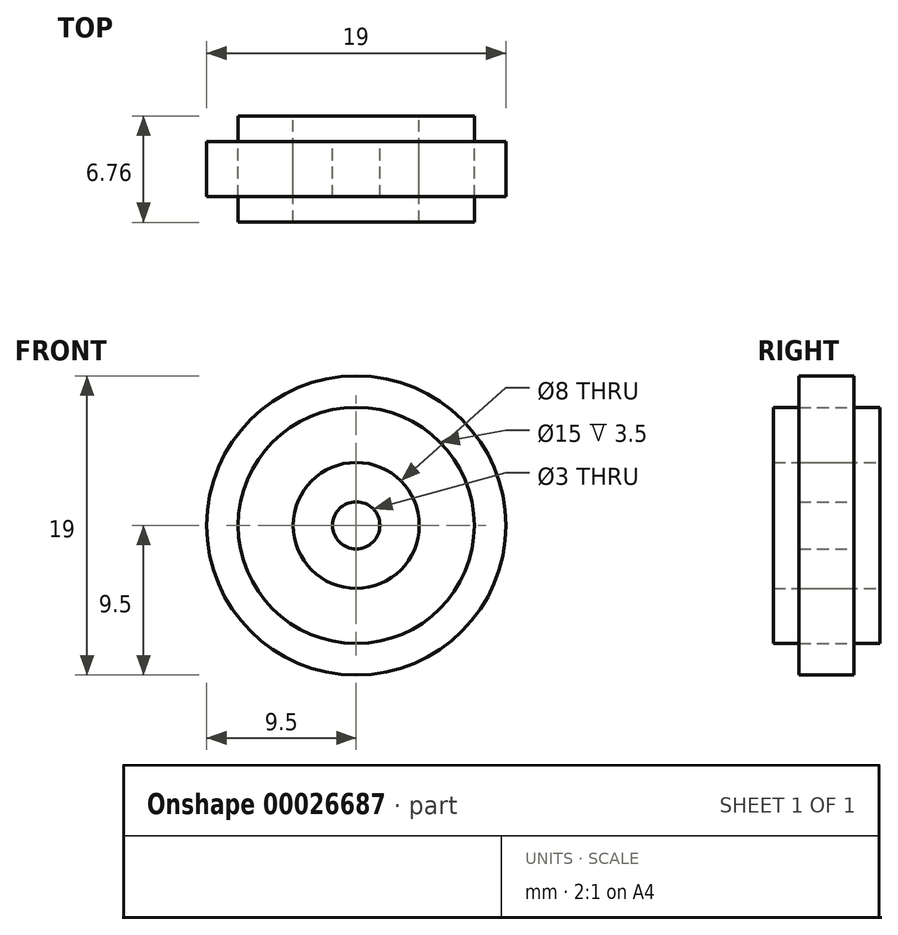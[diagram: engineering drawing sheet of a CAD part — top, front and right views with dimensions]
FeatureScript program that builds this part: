
annotation { "Feature Type Name" : "Feature", "Feature Type Description" : "" }
export const myFeature = defineFeature(function(context is Context, id is Id, definition is map)
    precondition{}
    {
        {
            var Q0;
            Q0=qCreatedBy(makeId("Front.planeOp"),FACE);
            var sketch = newSketch(context, id + "F0", { "sketchPlane" : qUnion([Q0])});
            skCircle(sketch, "E0", {"center": v(0, 0) * mm, "radius": 9.5 * mm});
            skCircle(sketch, "E1", {"center": v(0, 0) * mm, "radius": 4 * mm});
            skCircle(sketch, "E2", {"center": v(0, 0) * mm, "radius": 1.5 * mm});
            skCircle(sketch, "E3", {"center": v(0, 0) * mm, "radius": 7.5 * mm});
            skSolve(sketch);
        }
        {
            var Q0;
            Q0=makeQuery(id+"F0.imprint","IMPRINT",FACE,{"disambiguationData":[TD([[makeQuery(id+"F0.imprint","IMPRINT",EDGE,{"derivedFrom":sQuery(id+"F0.wireOp",EDGE,"E1")}),1.0]])]});
            var Q1;
            Q1=makeQuery(id+"F0.imprint","IMPRINT",FACE,{"disambiguationData":[TD([[makeQuery(id+"F0.imprint","IMPRINT",EDGE,{"derivedFrom":sQuery(id+"F0.wireOp",EDGE,"E0")}),1.0]])]});
            extrude(context, id + "F1", {"entities" : qUnion([Q0, Q1]), "endBound" : BoundingType.SYMMETRIC, "depth" : 3.5 * mm});
        }
        {
            var Q0;
            Q0=makeQuery(id+"F0.imprint","IMPRINT",FACE,{"disambiguationData":[TD([[makeQuery(id+"F0.imprint","IMPRINT",EDGE,{"derivedFrom":sQuery(id+"F0.wireOp",EDGE,"E1")}),-1.0]])]});
            extrude(context, id + "F2", {"entities" : qUnion([Q0]), "endBound" : BoundingType.SYMMETRIC, "depth" : 7 * mm - ((1 / 4) * mm)});
        }
    });
